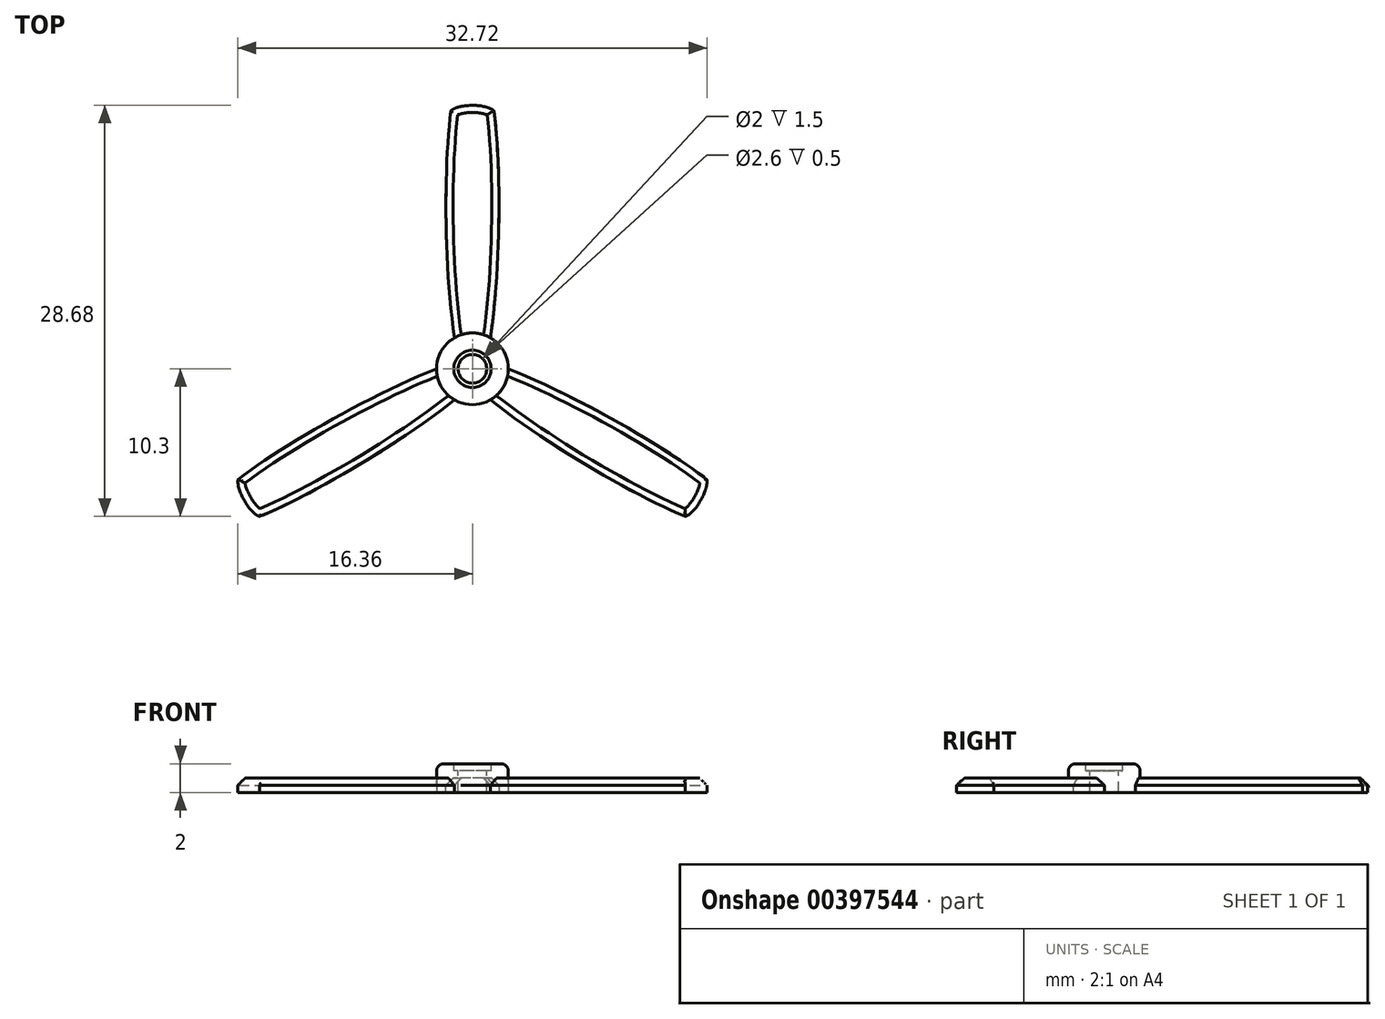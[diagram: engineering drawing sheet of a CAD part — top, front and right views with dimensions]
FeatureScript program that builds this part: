
annotation { "Feature Type Name" : "Feature", "Feature Type Description" : "" }
export const myFeature = defineFeature(function(context is Context, id is Id, definition is map)
    precondition{}
    {
        {
            var Q0;
            Q0=qCreatedBy(makeId("Top.planeOp"),FACE);
            var sketch = newSketch(context, id + "F0", { "sketchPlane" : qUnion([Q0])});
            skCircle(sketch, "E0", {"center": v(0, 0) * mm, "radius": 2.5 * mm});
            skLineSegment(sketch, "E1", {"start": v(0, 0) * mm, "end": v(0, 18.5) * mm, "construction": true});
            skLineSegment(sketch, "E2", {"start": v(-1.5, 18) * mm, "end": v(1.5, 18) * mm, "construction": true});
            skPoint(sketch, "E3", {"position": v(0, 18) * mm});
            skFitSpline(sketch, "E4", {"points": [v(-1.5, 18) * mm, v(1.5, 18) * mm], "startDerivative": vector(1.5, 1.5) * mm, "endDerivative": vector(1.5, -1.5) * mm});
            skFitSpline(sketch, "E5", {"points": [v(-1.5, 18) * mm, v(-1.25, 2.17) * mm], "startDerivative": vector(-1.5, -11.4) * mm, "endDerivative": vector(2.25, -15.1) * mm});
            skFitSpline(sketch, "E6.MirrorCS", {"points": [v(1.5, 18) * mm, v(1.25, 2.17) * mm], "startDerivative": vector(1.5, -11.4) * mm, "endDerivative": vector(-2.25, -15.1) * mm});
            skSolve(sketch);
        }
        {
            var Q0;
            Q0=makeQuery(id+"F0.imprint","IMPRINT",FACE,{"disambiguationData":[TD([[makeQuery(id+"F0.imprint","IMPRINT",EDGE,{"derivedFrom":sQuery(id+"F0.wireOp",EDGE,"E4")}),-1.0]])]});
            extrude(context, id + "F1", {"entities" : qUnion([Q0]), "depth" : 1 * mm});
        }
        {
            var Q0;
            {var subQ0=sQuery(id+"F0.wireOp",EDGE,"E0");var subQ1=makeQuery(id+"F0.imprint","INTERSECT",VERTEX,{"derivedFrom":[subQ0,sQuery(id+"F0.wireOp",EDGE,"E5")]});Q0=makeQuery(id+"F0.imprint","IMPRINT",FACE,{"disambiguationData":[TD([[makeQuery(id+"F0.imprint","IMPRINT",EDGE,{"disambiguationData":[TD([[subQ1,1.0]])],"derivedFrom":subQ0}),1.0]])]});}
            extrude(context, id + "F2", {"entities" : qUnion([Q0]), "operationType" : NewBodyOperationType.ADD, "depth" : 2 * mm});
        }
        {
            var Q0;
            Q0=makeQuery(id+"F1.opExtrude","SWEPT_BODY",BODY,{"disambiguationData":[OSD([sQuery(id+"F0.wireOp",EDGE,"E0"),sQuery(id+"F0.wireOp",EDGE,"E4"),sQuery(id+"F0.wireOp",EDGE,"E5"),sQuery(id+"F0.wireOp",EDGE,"E6.MirrorCS")])]});
            var Q1;
            Q1=sQuery(id+"F0.wireOp",EDGE,"E0");
            circularPattern(context, id + "F3", {"operationType" : NewBodyOperationType.ADD, "entities" : qUnion([Q0]), "axis" : qUnion([Q1]), "angle" : 360 * degree, "instanceCount" : 3, "equalSpace" : true});
        }
        {
            var Q0;
            Q0=makeQuery(id+"F2.opExtrude","CAP_EDGE",EDGE,{"disambiguationData":[OSD([sQuery(id+"F0.wireOp",EDGE,"E0")])],"isStart":false});
            fillet(context, id + "F4", {"entities" : qUnion([Q0]), "radius" : 0.5 * mm, "tangentPropagation" : true, "allowEdgeOverflow" : false});
        }
        {
            var Q0;
            Q0=makeQuery(id+"F3.opPattern","COPY",EDGE,{"derivedFrom":makeQuery(id+"F1.opExtrude","CAP_EDGE",EDGE,{"disambiguationData":[OSD([sQuery(id+"F0.wireOp",EDGE,"E4")])],"isStart":false}),"instanceName":"1"});
            var Q1;
            Q1=makeQuery(id+"F3.opPattern","COPY",EDGE,{"derivedFrom":makeQuery(id+"F1.opExtrude","CAP_EDGE",EDGE,{"disambiguationData":[OSD([sQuery(id+"F0.wireOp",EDGE,"E4")])],"isStart":false}),"instanceName":"2"});
            var Q2;
            Q2=makeQuery(id+"F3.opPattern","COPY",EDGE,{"derivedFrom":makeQuery(id+"F1.opExtrude","CAP_EDGE",EDGE,{"disambiguationData":[OSD([sQuery(id+"F0.wireOp",EDGE,"E6.MirrorCS")])],"isStart":false}),"instanceName":"2"});
            var Q3;
            Q3=makeQuery(id+"F3.opPattern","COPY",EDGE,{"derivedFrom":makeQuery(id+"F1.opExtrude","CAP_EDGE",EDGE,{"disambiguationData":[OSD([sQuery(id+"F0.wireOp",EDGE,"E5")])],"isStart":false}),"instanceName":"2"});
            var Q4;
            Q4=makeQuery(id+"F3.opPattern","COPY",EDGE,{"derivedFrom":makeQuery(id+"F1.opExtrude","CAP_EDGE",EDGE,{"disambiguationData":[OSD([sQuery(id+"F0.wireOp",EDGE,"E5")])],"isStart":false}),"instanceName":"1"});
            var Q5;
            Q5=makeQuery(id+"F3.opPattern","COPY",EDGE,{"derivedFrom":makeQuery(id+"F1.opExtrude","CAP_EDGE",EDGE,{"disambiguationData":[OSD([sQuery(id+"F0.wireOp",EDGE,"E6.MirrorCS")])],"isStart":false}),"instanceName":"1"});
            var Q6;
            Q6=makeQuery(id+"F1.opExtrude","CAP_EDGE",EDGE,{"disambiguationData":[OSD([sQuery(id+"F0.wireOp",EDGE,"E5")])],"isStart":false});
            var Q7;
            Q7=makeQuery(id+"F1.opExtrude","CAP_EDGE",EDGE,{"disambiguationData":[OSD([sQuery(id+"F0.wireOp",EDGE,"E6.MirrorCS")])],"isStart":false});
            var Q8;
            Q8=makeQuery(id+"F1.opExtrude","CAP_EDGE",EDGE,{"disambiguationData":[OSD([sQuery(id+"F0.wireOp",EDGE,"E4")])],"isStart":false});
            chamfer(context, id + "F5", {"entities" : qUnion([Q0, Q1, Q2, Q3, Q4, Q5, Q6, Q7, Q8]), "width" : 0.5 * mm, "tangentPropagation" : true});
        }
        {
            var Q0;
            Q0=makeQuery(id+"F2.opExtrude","CAP_FACE",FACE,{"disambiguationData":[OSD([sQuery(id+"F0.wireOp",EDGE,"E0")])],"isStart":false});
            var sketch = newSketch(context, id + "F6", { "sketchPlane" : qUnion([Q0])});
            skPoint(sketch, "E7", {"position": v(0, 0) * mm});
            skSolve(sketch);
        }
        {
            var Q0;
            Q0=sQuery(id+"F6.wireOp",VERTEX,"E7");
            var Q1;
            Q1=makeQuery(id+"F1.opExtrude","SWEPT_BODY",BODY,{"disambiguationData":[OSD([sQuery(id+"F0.wireOp",EDGE,"E0"),sQuery(id+"F0.wireOp",EDGE,"E4"),sQuery(id+"F0.wireOp",EDGE,"E5"),sQuery(id+"F0.wireOp",EDGE,"E6.MirrorCS")])]});
            hole(context, id + "F7", {"style" : HoleStyle.C_BORE, "endStyle" : HoleEndStyle.THROUGH, "holeDiameter" : 2 * mm, "cBoreDiameter" : 2.6 * mm, "cBoreDepth" : 0.5 * mm, "isTappedThrough" : true, "tappedDepth" : 12 * mm, "tapClearance" : 3, "locations" : qUnion([Q0]), "scope" : qUnion([Q1])});
        }
    });
